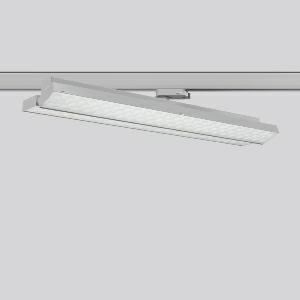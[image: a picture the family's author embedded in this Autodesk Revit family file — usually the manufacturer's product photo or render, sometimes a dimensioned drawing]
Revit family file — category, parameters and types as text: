
# Revit family: tx-move_742161_004_1_76_53b7
name_source: partatom
category: Lighting Fixtures
units: mm (PartAtom-declared; Revit-internal decimal feet)

## family parameters
Cut with Voids When Loaded = No
Host = Face
Light Source = No
Part Type = Normal
Room Calculation Point = No
Round Connector Dimension = Use Diameter
Shared = No

## types (1)
- MultiLumen 1 (1 x LED Modul 840, 3125 lm, 4000)
    Apparent Load = 41 VA
    CIE Flux Codes = 90 97 99 100 100
    Color Rendering = 80
    Color Temperature = 4000
    Default Elevation = 1800 mm
    Description = Series: TX-MOVE
Multifunctional surface-mounted spotlight for area lighting. Very flat design. Housing: sheet steel, powder-coated. Rotation range: 356°. Swivel range: 90°. Consistent alignment possible with visible tilt scale. High-efficiency LED units with optimum light control thanks to clear plastic (PC) lens optics. Spezielle Mikrostrukturen reduzieren Gelbsaum. Symmetrical light distribution. With adapter for RZB 3-circuit DALI tracks. Suitable for Track on ceiling. MultiLumen: Luminous flux adjustable in 3 steps. Factory setting is the highest luminous flux. Environmentally friendly and resource-saving due to replaceable and recyclable components. Very good glare control, ideal for till areas. 
Colour: silver, matt (approx. RAL 9006)
Length: 570 mm
Width: 119 mm
Height: 88 mm
Lamp: LED
Socket: without socket
Colour temperature: 4000K
Colour rendering index (CRI): 80
System power: 41 W
Rated luminous flux: 6250 lm
Luminous efficiency: 152 lm/W
System power 2: 57 W
Rated luminous flux 2: 8450 lm
Luminous efficiency 2: 148 lm/W
System power 3: 73 W
Rated luminous flux 3: 10400 lm
Luminous efficiency 3: 142 lm/W
Control gear: Dimmable EVG, DALI
Protection class: I
Type of protection: IP 20
    Height = 75 mm
    Lamp = 1 x LED Modul 840
    Lamp Light Flux = 3125 lm
    Lamp count = 1
    Length = 569 mm
    Lifetime = 50000 h
    Luminous efficacy = 152 lm/W
    Manufacturer = RZB
    ModVariant = No
    Model = 742161.004.1.76
    Mounting Place = Ceiling
    Mounting Type = Surface mounted
    Number of Poles = 1
    OnlyDefault = Yes
    Power Factor = 1
    Product Name = TX-MOVE
    Product group = Track mounted projectors
    ProductGroupID = 301
    Protection Class = Protection class I
    Protection Degree = IP 20
    RLX_Detail_Level = 1
    RLX_Emergency_Light_Flux = 0 lm
    RLX_Emergency_Type = 0
    RLX_Emergency_Type_DB = No
    RlxData = <blob elided: 33345 chars, md5=5f9b20cf>
    Socket = socket
    Standby Power = 0 W
    System Light Flux = 6250 lm
    System Power = 41 W
    Type Comments = MultiLumen 1
    Type Image = 742162.004.jpg
    URL = http://relux.com
    VarID = multilumen_1
    Voltage = 0 V
    Weight = 0.00 kg
    Width = 119 mm

## geometry (parser evidence)
native form markers: Blend x4, Sweep x14
no freeform markers — native parametric forms only
